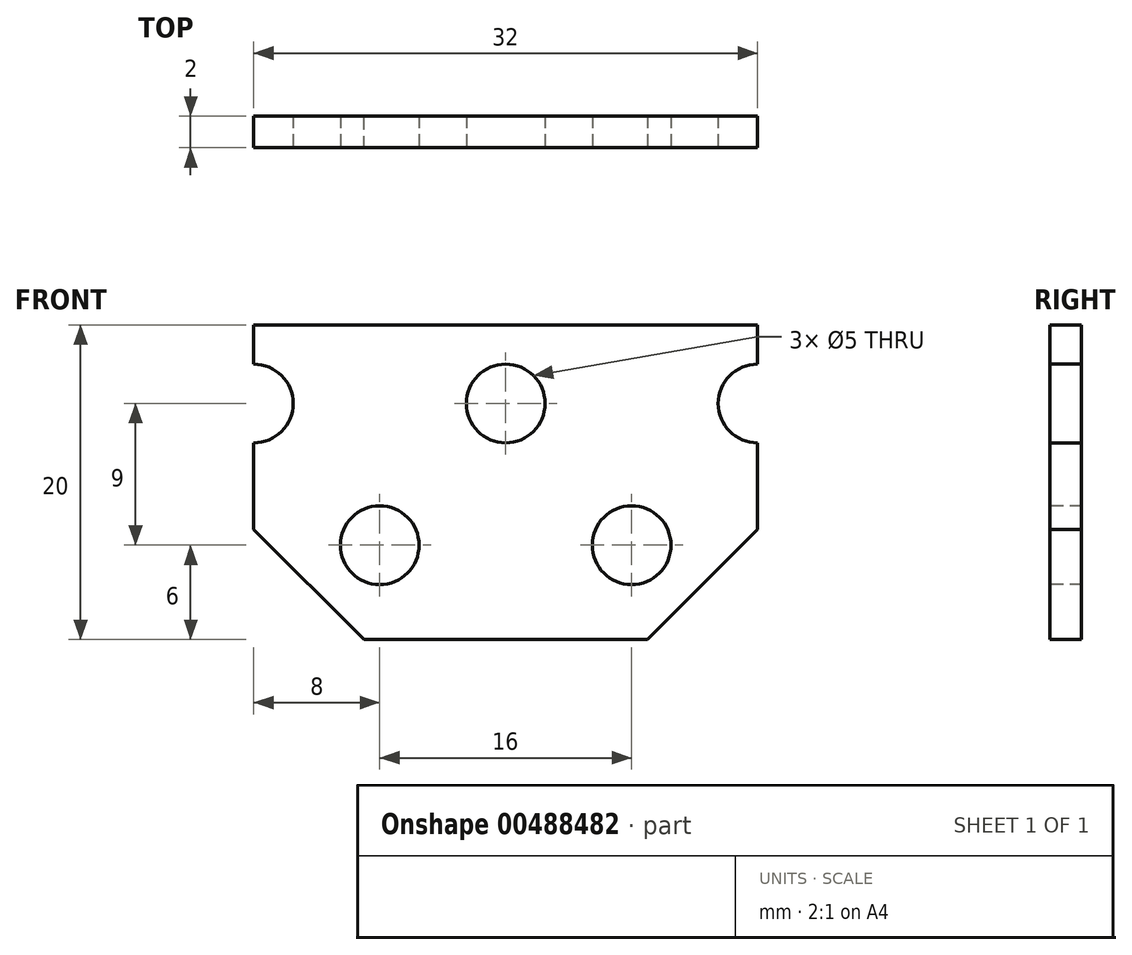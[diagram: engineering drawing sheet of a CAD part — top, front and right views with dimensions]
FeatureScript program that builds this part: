
annotation { "Feature Type Name" : "Feature", "Feature Type Description" : "" }
export const myFeature = defineFeature(function(context is Context, id is Id, definition is map)
    precondition{}
    {
        {
            var Q0;
            Q0=qCreatedBy(makeId("Front.planeOp"),FACE);
            var sketch = newSketch(context, id + "F0", { "sketchPlane" : qUnion([Q0])});
            skLineSegment(sketch, "E0.bottom", {"start": v(16, -10) * mm, "end": v(-16, -10) * mm});
            skLineSegment(sketch, "E0.top", {"start": v(16, 10) * mm, "end": v(-16, 10) * mm});
            skLineSegment(sketch, "E0.left", {"start": v(16, -10) * mm, "end": v(16, 10) * mm});
            skLineSegment(sketch, "E0.right", {"start": v(-16, -10) * mm, "end": v(-16, 10) * mm});
            skPoint(sketch, "E0.middle", {"position": v(0, 0) * mm});
            skSolve(sketch);
        }
        {
            var Q0;
            Q0=makeQuery(id+"F0.imprint","IMPRINT",FACE,{"disambiguationData":[TD([[makeQuery(id+"F0.imprint","IMPRINT",EDGE,{"derivedFrom":sQuery(id+"F0.wireOp",EDGE,"E0.bottom")}),-1.0]])]});
            extrude(context, id + "F1", {"entities" : qUnion([Q0]), "depth" : 2 * mm});
        }
        {
            var Q0;
            Q0=makeQuery(id+"F1.opExtrude","SWEPT_EDGE",EDGE,{"disambiguationData":[OSD([sQuery(id+"F0.wireOp",EDGE,"E0.bottom"),sQuery(id+"F0.wireOp",EDGE,"E0.right")])]});
            var Q1;
            Q1=makeQuery(id+"F1.opExtrude","SWEPT_EDGE",EDGE,{"disambiguationData":[OSD([sQuery(id+"F0.wireOp",EDGE,"E0.bottom"),sQuery(id+"F0.wireOp",EDGE,"E0.left")])]});
            chamfer(context, id + "F2", {"entities" : qUnion([Q0, Q1]), "width" : 7 * mm, "tangentPropagation" : true});
        }
        {
            var Q0;
            Q0=makeQuery(id+"F1.opExtrude","CAP_FACE",FACE,{"disambiguationData":[OSD([sQuery(id+"F0.wireOp",EDGE,"E0.bottom"),sQuery(id+"F0.wireOp",EDGE,"E0.top"),sQuery(id+"F0.wireOp",EDGE,"E0.left"),sQuery(id+"F0.wireOp",EDGE,"E0.right")])],"isStart":false});
            var sketch = newSketch(context, id + "F3", { "sketchPlane" : qUnion([Q0])});
            skCircle(sketch, "E1", {"center": v(-8, -4) * mm, "radius": 2.5 * mm});
            skCircle(sketch, "E2", {"center": v(8, -4) * mm, "radius": 2.5 * mm});
            skCircle(sketch, "E3", {"center": v(0, 5) * mm, "radius": 2.5 * mm});
            skCircle(sketch, "E4", {"center": v(-16, 5) * mm, "radius": 2.5 * mm});
            skCircle(sketch, "E5", {"center": v(16, 5) * mm, "radius": 2.5 * mm});
            skSolve(sketch);
        }
        {
            var Q0;
            {var subQ0=sQuery(id+"F3.wireOp",EDGE,"E4");var subQ1=makeQuery(id+"F1.opExtrude","CAP_EDGE",EDGE,{"disambiguationData":[OSD([sQuery(id+"F0.wireOp",EDGE,"E0.right")])],"isStart":false});var subQ2=makeQuery(id+"F3.imprint","INTERSECT",VERTEX,{"disambiguationData":[OD(0.0)],"derivedFrom":[subQ1,subQ0]});Q0=makeQuery(id+"F3.imprint","IMPRINT",FACE,{"disambiguationData":[TD([[makeQuery(id+"F3.imprint","IMPRINT",EDGE,{"disambiguationData":[TD([[subQ2,1.0]])],"derivedFrom":subQ0}),1.0]])]});}
            var Q1;
            Q1=makeQuery(id+"F3.imprint","IMPRINT",FACE,{"disambiguationData":[TD([[makeQuery(id+"F3.imprint","IMPRINT",EDGE,{"derivedFrom":sQuery(id+"F3.wireOp",EDGE,"E3")}),1.0]])]});
            var Q2;
            Q2=makeQuery(id+"F3.imprint","IMPRINT",FACE,{"disambiguationData":[TD([[makeQuery(id+"F3.imprint","IMPRINT",EDGE,{"derivedFrom":sQuery(id+"F3.wireOp",EDGE,"E1")}),1.0]])]});
            var Q3;
            Q3=makeQuery(id+"F3.imprint","IMPRINT",FACE,{"disambiguationData":[TD([[makeQuery(id+"F3.imprint","IMPRINT",EDGE,{"derivedFrom":sQuery(id+"F3.wireOp",EDGE,"E2")}),1.0]])]});
            var Q4;
            {var subQ0=sQuery(id+"F3.wireOp",EDGE,"E5");var subQ1=makeQuery(id+"F1.opExtrude","CAP_EDGE",EDGE,{"disambiguationData":[OSD([sQuery(id+"F0.wireOp",EDGE,"E0.left")])],"isStart":false});var subQ2=makeQuery(id+"F3.imprint","INTERSECT",VERTEX,{"disambiguationData":[OD(0.0)],"derivedFrom":[subQ1,subQ0]});Q4=makeQuery(id+"F3.imprint","IMPRINT",FACE,{"disambiguationData":[TD([[makeQuery(id+"F3.imprint","IMPRINT",EDGE,{"disambiguationData":[TD([[subQ2,-1.0]])],"derivedFrom":subQ0}),1.0]])]});}
            extrude(context, id + "F4", {"entities" : qUnion([Q0, Q1, Q2, Q3, Q4]), "operationType" : NewBodyOperationType.REMOVE, "oppositeDirection" : true, "depth" : 25 * mm});
        }
    });
